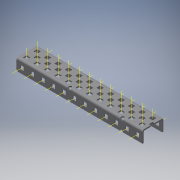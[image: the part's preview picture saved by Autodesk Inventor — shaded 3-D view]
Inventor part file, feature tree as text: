
AUTODESK INVENTOR PART (.ipt)
format: ipt  version: 2017 SP1 (Build 210196100, 196)  size: 1,973,760 bytes
history: native  units: in
note: dims shown in document units (in); Inventor stores cm internally (conversion verified against a paired STEP export)
features: other x66, pattern_linear x3, sheet_metal_op x1, extrude x1, imported_body x1, sketch x1
ambient origin geometry x8: Origin, YZ Plane, XZ Plane, XY Plane, X Axis, Y Axis, Z Axis, Center Point
bodies: Body1 (feature_tree)
feature tree (73):
  sheet_metal_op  "Fold1"
  other  "C-Channel"
  extrude  "length cut"  Depth=0.5in
  other  "top axis"
  other  "inner axis"
  other  "front axis"
  other  "back axis"
  pattern_linear  "top axes"  Spacing1=0.5in  [1 undecoded]
  pattern_linear  "inner axes"  Spacing1=0.5in  [1 undecoded]
  pattern_linear  "horiz axes"  Spacing1=-6.0in  [1 undecoded]
  other  "right plane"
  imported_body  "Base1"
  sketch  "Sketch1"  dims[d1=0.0in d4=0.5in d5=0.7874in d7=0.5in d10=0.5in d13=0.5in d14=-6.0in d15=0.0in d16=0.0in d17=0.0in d18=0.0in d19=0.0in]
  other  "Work Point1"
  other  "Work Point2"
  other  "Work Point3"
  other  "Work Point4"
  other  "Work Axis5"
  other  "Work Axis6"
  other  "Work Axis7"
  other  "Work Axis8"
  other  "Work Axis11"
  other  "Work Axis12"
  other  "Work Axis13"
  other  "Work Axis14"
  other  "Work Axis15"
  other  "Work Axis18"
  other  "Work Axis19"
  other  "Work Axis20"
  other  "Work Axis23"
  other  "Work Axis24"
  other  "Work Axis25"
  other  "Work Axis26"
  other  "Work Axis30"
  other  "Work Axis31"
  other  "Work Axis32"
  other  "Work Axis33"
  other  "left plane"
  other  "Work Axis37"
  other  "Work Axis38"
  other  "Work Axis39"
  other  "Work Axis40"
  other  "Work Axis41"
  other  "Work Axis42"
  other  "Work Axis57"
  other  "Work Axis58"
  other  "Work Axis59"
  other  "Work Axis60"
  other  "Work Axis61"
  other  "Work Axis62"
  other  "Work Axis77"
  other  "Work Axis78"
  other  "Work Axis79"
  other  "Work Axis80"
  other  "Work Axis81"
  other  "Work Axis82"
  other  "Work Axis97"
  other  "Work Axis98"
  other  "Work Axis99"
  other  "Work Axis100"
  other  "Work Axis101"
  other  "Work Axis102"
  other  "Work Axis117"
  other  "Work Axis118"
  other  "Work Axis119"
  other  "Work Axis120"
  other  "Work Axis121"
  other  "Work Axis122"
  other  "Work Axis137"
  other  "Work Axis138"
  other  "Work Axis139"
  other  "Work Axis140"
  other  "Work Axis141"
note: 3 required parameter values undecoded (feature->parameter linkage not recoverable at this tier; creation-order binding heuristic only, values carry confidence <= 0.55)
